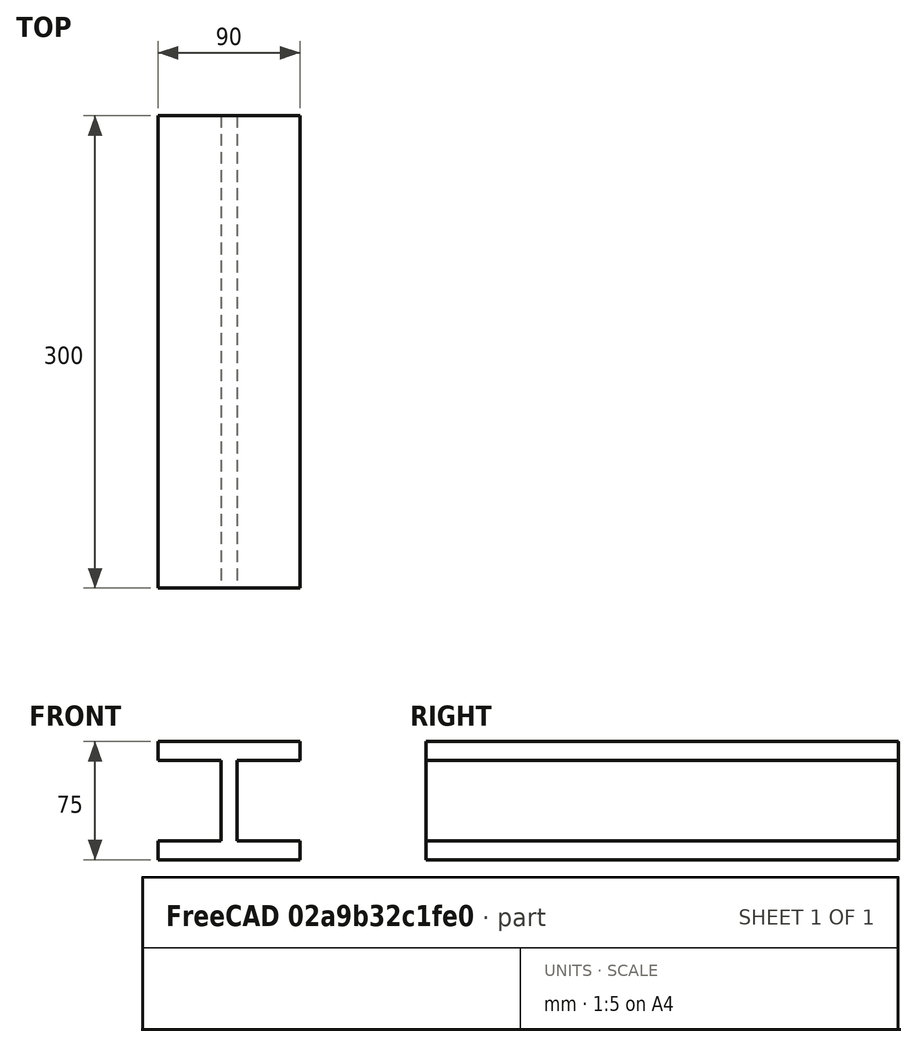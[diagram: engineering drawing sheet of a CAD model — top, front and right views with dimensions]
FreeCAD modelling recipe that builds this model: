
FCSTD DOCUMENT  (FreeCAD 0.16R6707 (Git))
Label: 03-01-viga-H
License: All rights reserved
LicenseURL: http://en.wikipedia.org/wiki/All_rights_reserved
objects: Sketcher::SketchObject×1, PartDesign::Pad×1
note: 3 computed .brp shape members not serialized (recipe doc carries the construction recipe); baked Part::Feature solids carry a one-line shape summary decoded from their .brp

FEATURE [Sketcher::SketchObject] Sketch  label="Boceto-viga-H"
  Placement = pos=(0,0,0) rot=(1,0,0;1.5708rad)
  sketch-geometry (12):
    g0: LineSegment StartX=0 StartY=75 StartZ=0 EndX=90 EndY=75 EndZ=0
    g1: LineSegment StartX=90 StartY=75 StartZ=0 EndX=90 EndY=63 EndZ=0
    g2: LineSegment StartX=90 StartY=63 StartZ=0 EndX=50 EndY=63 EndZ=0
    g3: LineSegment StartX=50 StartY=63 StartZ=0 EndX=50 EndY=12 EndZ=0
    g4: LineSegment StartX=50 StartY=12 StartZ=0 EndX=90 EndY=12 EndZ=0
    g5: LineSegment StartX=90 StartY=12 StartZ=0 EndX=90 EndY=0 EndZ=0
    g6: LineSegment StartX=90 StartY=0 StartZ=0 EndX=0 EndY=0 EndZ=0
    g7: LineSegment StartX=0 StartY=0 StartZ=0 EndX=0 EndY=12 EndZ=0
    g8: LineSegment StartX=0 StartY=12 StartZ=0 EndX=40 EndY=12 EndZ=0
    g9: LineSegment StartX=40 StartY=12 StartZ=0 EndX=40 EndY=63 EndZ=0
    g10: LineSegment StartX=40 StartY=63 StartZ=0 EndX=0 EndY=63 EndZ=0
    g11: LineSegment StartX=0 StartY=63 StartZ=0 EndX=0 EndY=75 EndZ=0
  constraints (35):
    c: Horizontal(g0)
    c: Coincident(g0,g1)
    c: Vertical(g1)
    c: Coincident(g1,g2)
    c: Horizontal(g2)
    c: Coincident(g2,g3)
    c: Vertical(g3)
    c: Coincident(g3,g4)
    c: Horizontal(g4)
    c: Coincident(g4,g5)
    c: Vertical(g5)
    c: Coincident(g5,g6)
    c: Horizontal(g6)
    c: Coincident(g6,g7)
    c: Coincident(g7,g8)
    c: Horizontal(g8)
    c: Coincident(g8,g9)
    c: Vertical(g9)
    c: Coincident(g9,g10)
    c: Horizontal(g10)
    c: Coincident(g10,g11)
    c: Coincident(g11,g0)
    c: Vertical(g11)
    c: Vertical(g7)
    c: Equal(g0,g6)
    c: Equal(g10,g2)
    c: DistanceX(g9,g2) = 10
    c: Equal(g8,g4)
    c: Coincident(g6,g-1)
    c: DistanceY(g-1,g0) = 75
    c: DistanceX(g-1,g5) = 90
    c: DistanceY(g5,g5) = 12
    c: Equal(g11,g1)
    c: Equal(g1,g5)
    c: Equal(g5,g7)
FEATURE [PartDesign::Pad] Pad  label="Viga-H"
  Length = 300
  Length2 = 100
  Placement = pos=(0,0,0) rot=(1,0,0;1.5708rad)
  Sketch = -> Sketch
  Type = 0
